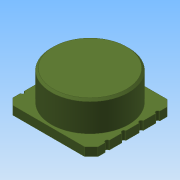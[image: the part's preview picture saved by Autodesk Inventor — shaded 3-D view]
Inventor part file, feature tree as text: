
AUTODESK INVENTOR PART (.ipt)
format: ipt  version: 2015 (Build 190159000, 159)  size: 276,992 bytes
history: native  units: mm
features: sketch x4, extrude x3, chamfer x2, fillet x1, projected_geometry x1
ambient origin geometry x8: Origin, YZ Plane, XZ Plane, XY Plane, X Axis, Y Axis, Z Axis, Center Point
bodies: Volumenkörper1 (feature_tree)
feature tree (11):
  extrude  "Extrusion1"  TaperAngle=0.0deg  [1 undecoded]
  extrude  "Extrusion3"  Depth=1.2mm
  extrude  "Extrusion2"  Depth=1.3mm
  sketch  "Skizze5"  dims[d11=1.25mm d12=2.245mm d13=0.0mm d14=0.382205mm d15=0.931133mm d16=0.375203mm d17=0.501621mm d18=0.5mm d19=2.0mm d20=45.0deg d21=0.15mm d22=2.0mm d23=45.0deg d24=0.001mm]
  chamfer  "Fase1"  Distance=2.245mm
  chamfer  "Fase2"  [1 undecoded]
  fillet  "Rundung1"  Radius=0.382205mm
  sketch  "Skizze1"  dims[d3=0.0mm d6=0.0mm]
  sketch  "Skizze2"  dims[d7=0.15mm d8=1.2mm]
  sketch  "Skizze3"  dims[d9=1.25mm d10=1.3mm]
  projected_geometry  "Projizierte Kontur1"
note: 2 required parameter values undecoded (feature->parameter linkage not recoverable at this tier; creation-order binding heuristic only, values carry confidence <= 0.55)
